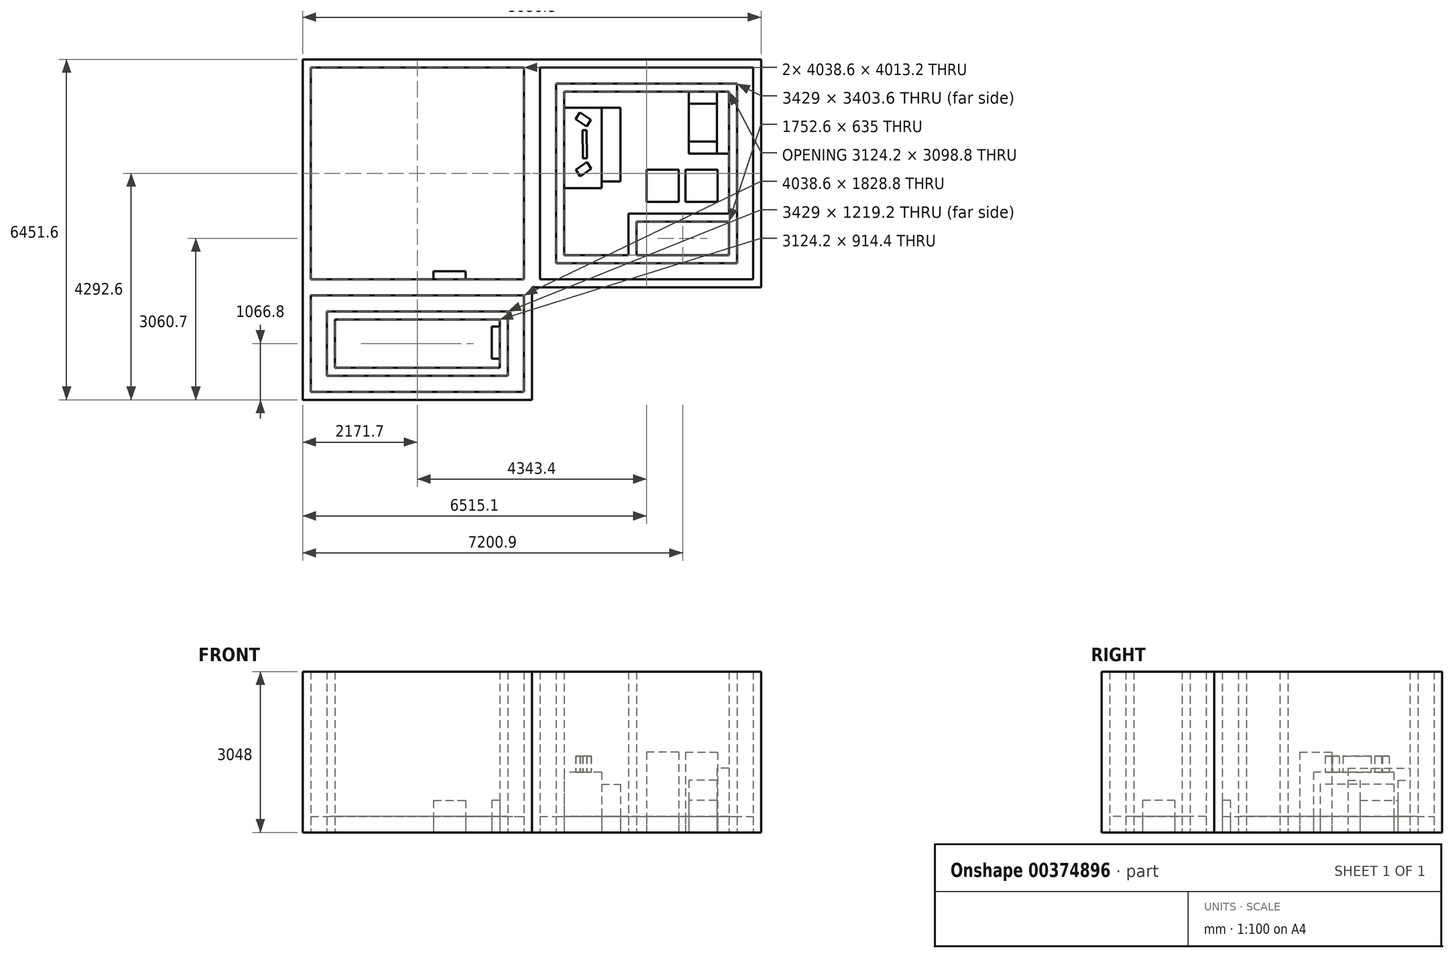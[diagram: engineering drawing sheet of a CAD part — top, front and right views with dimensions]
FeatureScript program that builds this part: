
annotation { "Feature Type Name" : "Feature", "Feature Type Description" : "" }
export const myFeature = defineFeature(function(context is Context, id is Id, definition is map)
    precondition{}
    {
        {
            var Q0;
            Q0=qCreatedBy(makeId("Top.planeOp"),FACE);
            var sketch = newSketch(context, id + "F0", { "sketchPlane" : qUnion([Q0])});
            skLineSegment(sketch, "E0.bottom", {"start": v(1562.1, 1549.4) * mm, "end": v(-1562.1, 1549.4) * mm});
            skLineSegment(sketch, "E0.top", {"start": v(1562.1, -1549.4) * mm, "end": v(-1562.1, -1549.4) * mm});
            skLineSegment(sketch, "E0.left", {"start": v(1562.1, 1549.4) * mm, "end": v(1562.1, -1549.4) * mm});
            skLineSegment(sketch, "E0.right", {"start": v(-1562.1, 1549.4) * mm, "end": v(-1562.1, -1549.4) * mm});
            skPoint(sketch, "E0.middle", {"position": v(0, 0) * mm});
            skLineSegment(sketch, "E1", {"start": v(-342.9, -762) * mm, "end": v(-342.9, -1549.4) * mm});
            skLineSegment(sketch, "E2", {"start": v(-190.5, -914.4) * mm, "end": v(-190.5, -1549.4) * mm});
            skLineSegment(sketch, "E3", {"start": v(-1714.5, 1701.8) * mm, "end": v(1714.5, 1701.8) * mm});
            skLineSegment(sketch, "E4", {"start": v(-1714.5, 1701.8) * mm, "end": v(-1714.5, -1701.8) * mm});
            skLineSegment(sketch, "E5", {"start": v(-1714.5, -1701.8) * mm, "end": v(1714.5, -1701.8) * mm});
            skLineSegment(sketch, "E6", {"start": v(1714.5, -1701.8) * mm, "end": v(1714.5, 1701.8) * mm});
            skLineSegment(sketch, "E7", {"start": v(-342.9, -762) * mm, "end": v(1562.1, -762) * mm});
            skLineSegment(sketch, "E8", {"start": v(-190.5, -914.4) * mm, "end": v(1562.1, -914.4) * mm});
            skLineSegment(sketch, "E9", {"start": v(-1562.1, 1244.6) * mm, "end": v(-850.9, 1244.6) * mm});
            skLineSegment(sketch, "E10", {"start": v(-850.9, 1244.6) * mm, "end": v(-850.9, -279.4) * mm});
            skLineSegment(sketch, "E11", {"start": v(-850.9, -279.4) * mm, "end": v(-1562.1, -279.4) * mm});
            skLineSegment(sketch, "E12", {"start": v(-850.9, 1244.6) * mm, "end": v(-495.3, 1244.6) * mm});
            skLineSegment(sketch, "E13", {"start": v(-495.3, 1244.6) * mm, "end": v(-495.3, -152.4) * mm});
            skPoint(sketch, "E14.endSnap0", {"position": v(-495.3, 546.1) * mm});
            skLineSegment(sketch, "E15", {"start": v(-1049.68, 1012.65) * mm, "end": v(-1260.14, 1154.85) * mm});
            skLineSegment(sketch, "E16", {"start": v(-1260.14, 1154.85) * mm, "end": v(-1345.47, 1028.58) * mm});
            skLineSegment(sketch, "E17", {"start": v(-1345.47, 1028.58) * mm, "end": v(-1135, 886.37) * mm});
            skLineSegment(sketch, "E18", {"start": v(-1135, 886.37) * mm, "end": v(-1049.68, 1012.65) * mm});
            skLineSegment(sketch, "E19", {"start": v(-1041.93, 84.79) * mm, "end": v(-1252.4, -57.42) * mm});
            skLineSegment(sketch, "E20", {"start": v(-1252.4, -57.42) * mm, "end": v(-1337.71, 68.86) * mm});
            skLineSegment(sketch, "E21", {"start": v(-1337.71, 68.86) * mm, "end": v(-1127.25, 211.07) * mm});
            skLineSegment(sketch, "E22", {"start": v(-1127.25, 211.07) * mm, "end": v(-1041.93, 84.79) * mm});
            skLineSegment(sketch, "E23", {"start": v(-495.3, -152.4) * mm, "end": v(-850.9, -152.4) * mm});
            skLineSegment(sketch, "E24", {"start": v(-2019.3, -2006.6) * mm, "end": v(2019.3, -2006.6) * mm});
            skLineSegment(sketch, "E25", {"start": v(-2019.3, -2006.6) * mm, "end": v(-2019.3, 2006.6) * mm});
            skLineSegment(sketch, "E26", {"start": v(-2019.3, 2006.6) * mm, "end": v(2019.3, 2006.6) * mm});
            skLineSegment(sketch, "E27", {"start": v(2019.3, 2006.6) * mm, "end": v(2019.3, -2006.6) * mm});
            skLineSegment(sketch, "E28", {"start": v(-2171.7, 2159) * mm, "end": v(-2171.7, -2159) * mm});
            skLineSegment(sketch, "E29", {"start": v(-2171.7, -2159) * mm, "end": v(2171.7, -2159) * mm});
            skLineSegment(sketch, "E30", {"start": v(-2171.7, 2159) * mm, "end": v(2171.7, 2159) * mm});
            skLineSegment(sketch, "E31", {"start": v(2171.7, 2159) * mm, "end": v(2171.7, -2159) * mm});
            skLineSegment(sketch, "E32", {"start": v(0, -539.49) * mm, "end": v(0, 70.11) * mm});
            skLineSegment(sketch, "E33", {"start": v(0, 70.11) * mm, "end": v(609.6, 70.11) * mm});
            skLineSegment(sketch, "E34", {"start": v(609.6, 70.11) * mm, "end": v(609.6, -539.49) * mm});
            skLineSegment(sketch, "E35", {"start": v(609.6, -539.49) * mm, "end": v(0, -539.49) * mm});
            skLineSegment(sketch, "E36", {"start": v(736.6, 70.11) * mm, "end": v(736.6, -539.49) * mm});
            skLineSegment(sketch, "E37", {"start": v(736.6, -539.49) * mm, "end": v(1346.2, -539.49) * mm});
            skLineSegment(sketch, "E38", {"start": v(736.6, 70.11) * mm, "end": v(1346.2, 70.11) * mm});
            skLineSegment(sketch, "E39", {"start": v(1346.2, 70.11) * mm, "end": v(1346.2, -539.49) * mm});
            skLineSegment(sketch, "E40", {"start": v(1562.1, 374.91) * mm, "end": v(800.1, 374.91) * mm});
            skLineSegment(sketch, "E41", {"start": v(800.1, 374.91) * mm, "end": v(800.1, 1549.4) * mm});
            skLineSegment(sketch, "E42", {"start": v(1333.5, 374.91) * mm, "end": v(1333.5, 1549.4) * mm});
            skLineSegment(sketch, "E43", {"start": v(1333.5, 1320.8) * mm, "end": v(800.1, 1320.8) * mm});
            skLineSegment(sketch, "E44", {"start": v(1333.5, 603.51) * mm, "end": v(800.1, 603.51) * mm});
            skLineSegment(sketch, "E45", {"start": v(-2171.7, 2159) * mm, "end": v(-6515.1, 2159) * mm});
            skLineSegment(sketch, "E46", {"start": v(-6515.1, 2159) * mm, "end": v(-6515.1, -2159) * mm});
            skLineSegment(sketch, "E47", {"start": v(-6515.1, -2159) * mm, "end": v(-2171.7, -2159) * mm});
            skLineSegment(sketch, "E48", {"start": v(-6362.7, 2006.6) * mm, "end": v(-6362.7, -2006.6) * mm});
            skLineSegment(sketch, "E49", {"start": v(-2324.1, -2006.6) * mm, "end": v(-2324.1, 2006.6) * mm});
            skLineSegment(sketch, "E50", {"start": v(-6362.7, 2006.6) * mm, "end": v(-2324.1, 2006.6) * mm});
            skLineSegment(sketch, "E51", {"start": v(-6362.7, -2006.6) * mm, "end": v(-2324.1, -2006.6) * mm});
            skLineSegment(sketch, "E52", {"start": v(-6515.1, -2159) * mm, "end": v(-6515.1, -4292.6) * mm});
            skLineSegment(sketch, "E53", {"start": v(-2171.7, -2159) * mm, "end": v(-2171.7, -4292.6) * mm});
            skLineSegment(sketch, "E54", {"start": v(-6515.1, -4292.6) * mm, "end": v(-2171.7, -4292.6) * mm});
            skLineSegment(sketch, "E55", {"start": v(-2324.1, -2311.4) * mm, "end": v(-2324.1, -4140.2) * mm});
            skLineSegment(sketch, "E56", {"start": v(-2324.1, -2311.4) * mm, "end": v(-6362.7, -2311.4) * mm});
            skLineSegment(sketch, "E57", {"start": v(-2324.1, -4140.2) * mm, "end": v(-6362.7, -4140.2) * mm});
            skLineSegment(sketch, "E58", {"start": v(-6362.7, -4140.2) * mm, "end": v(-6362.7, -2311.4) * mm});
            skLineSegment(sketch, "E59", {"start": v(-2628.9, -2616.2) * mm, "end": v(-6057.9, -2616.2) * mm});
            skLineSegment(sketch, "E60", {"start": v(-2628.9, -3835.4) * mm, "end": v(-6057.9, -3835.4) * mm});
            skLineSegment(sketch, "E61", {"start": v(-6057.9, -2616.2) * mm, "end": v(-6057.9, -3835.4) * mm});
            skLineSegment(sketch, "E62", {"start": v(-2628.9, -2616.2) * mm, "end": v(-2628.9, -3835.4) * mm});
            skLineSegment(sketch, "E63", {"start": v(-2781.3, -2768.6) * mm, "end": v(-5905.5, -2768.6) * mm});
            skLineSegment(sketch, "E64", {"start": v(-2781.3, -3683) * mm, "end": v(-5905.5, -3683) * mm});
            skLineSegment(sketch, "E65", {"start": v(-5905.5, -3683) * mm, "end": v(-5905.5, -2768.6) * mm});
            skLineSegment(sketch, "E66", {"start": v(-2781.3, -2768.6) * mm, "end": v(-2781.3, -3683) * mm});
            skLineSegment(sketch, "E67", {"start": v(-1134.2, 815.38) * mm, "end": v(-1128.07, 282.06) * mm});
            skLineSegment(sketch, "E68", {"start": v(-1134.2, 815.38) * mm, "end": v(-1210.39, 814.5) * mm});
            skLineSegment(sketch, "E69", {"start": v(-1128.07, 282.06) * mm, "end": v(-1204.26, 281.18) * mm});
            skLineSegment(sketch, "E70", {"start": v(-1204.26, 281.18) * mm, "end": v(-1210.39, 814.5) * mm});
            skLineSegment(sketch, "E71", {"start": v(-3425.85, -2006.6) * mm, "end": v(-3425.85, -1854.2) * mm});
            skLineSegment(sketch, "E72", {"start": v(-3425.85, -1854.2) * mm, "end": v(-4035.45, -1854.2) * mm});
            skLineSegment(sketch, "E73", {"start": v(-4035.45, -1854.2) * mm, "end": v(-4035.45, -2006.6) * mm});
            skLineSegment(sketch, "E74", {"start": v(-2781.3, -2904.21) * mm, "end": v(-2933.7, -2904.21) * mm});
            skLineSegment(sketch, "E75", {"start": v(-2933.7, -2904.21) * mm, "end": v(-2933.7, -3513.81) * mm});
            skLineSegment(sketch, "E76", {"start": v(-2933.7, -3513.81) * mm, "end": v(-2781.3, -3513.81) * mm});
            skSolve(sketch);
        }
        {
            var Q0;
            Q0=makeQuery(id+"F0.imprint","IMPRINT",FACE,{"disambiguationData":[TD([[makeQuery(id+"F0.imprint","IMPRINT",EDGE,{"derivedFrom":sQuery(id+"F0.wireOp",EDGE,"E28")}),-1.0]])]});
            var Q1;
            Q1=makeQuery(id+"F0.imprint","IMPRINT",FACE,{"disambiguationData":[TD([[makeQuery(id+"F0.imprint","IMPRINT",EDGE,{"derivedFrom":sQuery(id+"F0.wireOp",EDGE,"E47")}),-1.0]])]});
            var Q2;
            Q2=makeQuery(id+"F0.imprint","IMPRINT",FACE,{"disambiguationData":[TD([[makeQuery(id+"F0.imprint","IMPRINT",EDGE,{"derivedFrom":sQuery(id+"F0.wireOp",EDGE,"E59")}),1.0]])]});
            var Q3;
            Q3=makeQuery(id+"F0.imprint","IMPRINT",FACE,{"disambiguationData":[TD([[makeQuery(id+"F0.imprint","IMPRINT",EDGE,{"derivedFrom":sQuery(id+"F0.wireOp",EDGE,"E24")}),-1.0]])]});
            var Q4;
            Q4=makeQuery(id+"F0.imprint","IMPRINT",FACE,{"disambiguationData":[TD([[makeQuery(id+"F0.imprint","IMPRINT",EDGE,{"derivedFrom":sQuery(id+"F0.wireOp",EDGE,"E3")}),-1.0]])]});
            var Q5;
            {var subQ0=sQuery(id+"F0.wireOp",EDGE,"E1");Q5=makeQuery(id+"F0.imprint","IMPRINT",FACE,{"disambiguationData":[TD([[makeQuery(id+"F0.imprint","IMPRINT",EDGE,{"derivedFrom":subQ0}),1.0]])]});}
            extrude(context, id + "F1", {"entities" : qUnion([Q0, Q1, Q2, Q3, Q4, Q5]), "depth" : 3048 * mm});
        }
        {
            var Q0;
            {var subQ5=sQuery(id+"F0.wireOp",EDGE,"E43");Q0=makeQuery(id+"F0.imprint","IMPRINT",FACE,{"disambiguationData":[TD([[makeQuery(id+"F0.imprint","IMPRINT",EDGE,{"derivedFrom":subQ5}),-1.0]])]});}
            var Q1;
            {var subQ5=sQuery(id+"F0.wireOp",EDGE,"E44");Q1=makeQuery(id+"F0.imprint","IMPRINT",FACE,{"disambiguationData":[TD([[makeQuery(id+"F0.imprint","IMPRINT",EDGE,{"derivedFrom":subQ5}),1.0]])]});}
            extrude(context, id + "F2", {"entities" : qUnion([Q0, Q1]), "depth" : 990.6 * mm});
        }
        {
            var Q0;
            {var subQ0=sQuery(id+"F0.wireOp",EDGE,"E43");Q0=makeQuery(id+"F0.imprint","IMPRINT",FACE,{"disambiguationData":[TD([[makeQuery(id+"F0.imprint","IMPRINT",EDGE,{"derivedFrom":subQ0}),1.0]])]});}
            extrude(context, id + "F3", {"entities" : qUnion([Q0]), "depth" : 609.6 * mm});
        }
        {
            var Q0;
            Q0=makeQuery(id+"F0.imprint","IMPRINT",FACE,{"disambiguationData":[TD([[makeQuery(id+"F0.imprint","IMPRINT",EDGE,{"derivedFrom":sQuery(id+"F0.wireOp",EDGE,"E32")}),-1.0]])]});
            var Q1;
            Q1=makeQuery(id+"F0.imprint","IMPRINT",FACE,{"disambiguationData":[TD([[makeQuery(id+"F0.imprint","IMPRINT",EDGE,{"derivedFrom":sQuery(id+"F0.wireOp",EDGE,"E36")}),1.0]])]});
            extrude(context, id + "F4", {"entities" : qUnion([Q0, Q1]), "depth" : 1524 * mm});
        }
        {
            var Q0;
            {var subQ0=sQuery(id+"F0.wireOp",EDGE,"E12");Q0=makeQuery(id+"F0.imprint","IMPRINT",FACE,{"disambiguationData":[TD([[makeQuery(id+"F0.imprint","IMPRINT",EDGE,{"derivedFrom":subQ0}),-1.0]])]});}
            extrude(context, id + "F5", {"entities" : qUnion([Q0]), "depth" : 914.4 * mm});
        }
        {
            var Q0;
            {var subQ1=sQuery(id+"F0.wireOp",EDGE,"E9");Q0=makeQuery(id+"F0.imprint","IMPRINT",FACE,{"disambiguationData":[TD([[makeQuery(id+"F0.imprint","IMPRINT",EDGE,{"derivedFrom":subQ1}),-1.0]])]});}
            extrude(context, id + "F6", {"entities" : qUnion([Q0]), "depth" : 1143 * mm});
        }
        {
            var Q0;
            Q0=makeQuery(id+"F0.imprint","IMPRINT",FACE,{"disambiguationData":[TD([[makeQuery(id+"F0.imprint","IMPRINT",EDGE,{"derivedFrom":sQuery(id+"F0.wireOp",EDGE,"E15")}),1.0]])]});
            var Q1;
            Q1=makeQuery(id+"F0.imprint","IMPRINT",FACE,{"disambiguationData":[TD([[makeQuery(id+"F0.imprint","IMPRINT",EDGE,{"derivedFrom":sQuery(id+"F0.wireOp",EDGE,"E67")}),-1.0]])]});
            var Q2;
            Q2=makeQuery(id+"F0.imprint","IMPRINT",FACE,{"disambiguationData":[TD([[makeQuery(id+"F0.imprint","IMPRINT",EDGE,{"derivedFrom":sQuery(id+"F0.wireOp",EDGE,"E19")}),-1.0]])]});
            extrude(context, id + "F7", {"entities" : qUnion([Q0, Q1, Q2]), "operationType" : NewBodyOperationType.ADD, "depth" : 1447.8 * mm});
        }
        {
            var Q0;
            {var subQ4=sQuery(id+"F0.wireOp",EDGE,"E0.left");var subQ6=sQuery(id+"F0.wireOp",EDGE,"E0.bottom");var subQ7=makeQuery(id+"F0.imprint","INTERSECT",VERTEX,{"derivedFrom":[subQ6,subQ4]});Q0=makeQuery(id+"F0.imprint","IMPRINT",FACE,{"disambiguationData":[TD([[makeQuery(id+"F0.imprint","IMPRINT",EDGE,{"disambiguationData":[TD([[subQ7,-1.0]])],"derivedFrom":subQ6}),1.0]])]});}
            extrude(context, id + "F8", {"entities" : qUnion([Q0]), "depth" : 1219.2 * mm});
        }
        {
            var Q0;
            {var subQ7=sQuery(id+"F0.wireOp",EDGE,"E1");Q0=makeQuery(id+"F0.imprint","IMPRINT",FACE,{"disambiguationData":[TD([[makeQuery(id+"F0.imprint","IMPRINT",EDGE,{"derivedFrom":subQ7}),-1.0]])]});}
            var Q1;
            {var subQ3=sQuery(id+"F0.wireOp",EDGE,"E2");Q1=makeQuery(id+"F0.imprint","IMPRINT",FACE,{"disambiguationData":[TD([[makeQuery(id+"F0.imprint","IMPRINT",EDGE,{"derivedFrom":subQ3}),1.0]])]});}
            var Q2;
            Q2=makeQuery(id+"F0.imprint","IMPRINT",FACE,{"disambiguationData":[TD([[makeQuery(id+"F0.imprint","IMPRINT",EDGE,{"derivedFrom":sQuery(id+"F0.wireOp",EDGE,"E3")}),1.0]])]});
            var Q3;
            Q3=makeQuery(id+"F0.imprint","IMPRINT",FACE,{"disambiguationData":[TD([[makeQuery(id+"F0.imprint","IMPRINT",EDGE,{"derivedFrom":sQuery(id+"F0.wireOp",EDGE,"E48")}),1.0]])]});
            var Q4;
            Q4=makeQuery(id+"F0.imprint","IMPRINT",FACE,{"disambiguationData":[TD([[makeQuery(id+"F0.imprint","IMPRINT",EDGE,{"derivedFrom":sQuery(id+"F0.wireOp",EDGE,"E63")}),1.0]])]});
            var Q5;
            Q5=makeQuery(id+"F0.imprint","IMPRINT",FACE,{"disambiguationData":[TD([[makeQuery(id+"F0.imprint","IMPRINT",EDGE,{"derivedFrom":sQuery(id+"F0.wireOp",EDGE,"E55")}),-1.0]])]});
            extrude(context, id + "F9", {"entities" : qUnion([Q0, Q1, Q2, Q3, Q4, Q5]), "depth" : 304.8 * mm});
        }
        {
            var Q0;
            {var subQ0=sQuery(id+"F0.wireOp",EDGE,"E71");Q0=makeQuery(id+"F0.imprint","IMPRINT",FACE,{"disambiguationData":[TD([[makeQuery(id+"F0.imprint","IMPRINT",EDGE,{"derivedFrom":subQ0}),1.0]])]});}
            var Q1;
            {var subQ0=sQuery(id+"F0.wireOp",EDGE,"E74");Q1=makeQuery(id+"F0.imprint","IMPRINT",FACE,{"disambiguationData":[TD([[makeQuery(id+"F0.imprint","IMPRINT",EDGE,{"derivedFrom":subQ0}),1.0]])]});}
            extrude(context, id + "F10", {"entities" : qUnion([Q0, Q1]), "depth" : 609.6 * mm});
        }
    });
